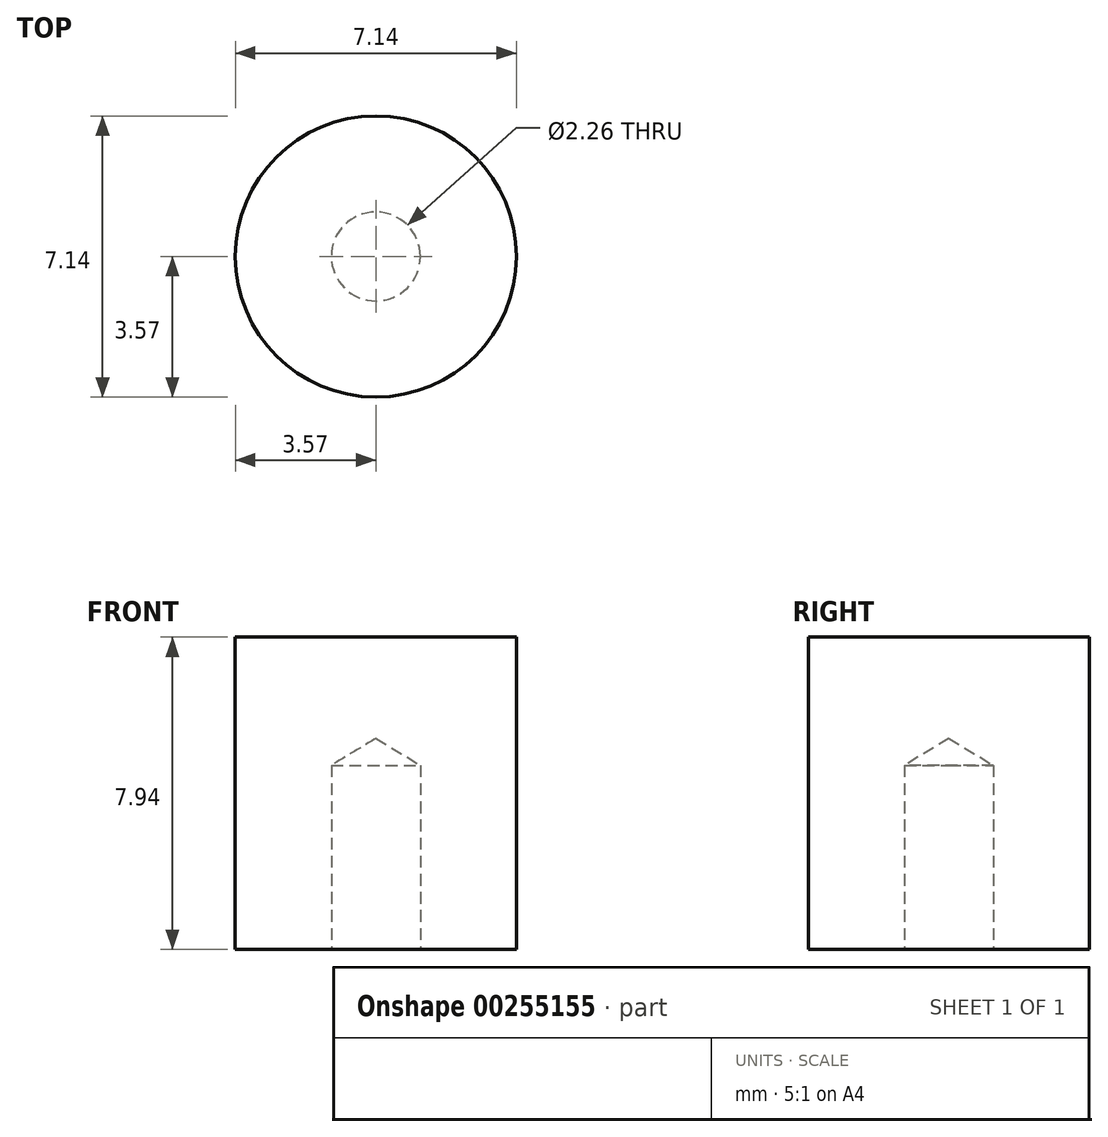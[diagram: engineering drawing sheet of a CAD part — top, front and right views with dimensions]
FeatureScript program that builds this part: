
annotation { "Feature Type Name" : "Feature", "Feature Type Description" : "" }
export const myFeature = defineFeature(function(context is Context, id is Id, definition is map)
    precondition{}
    {
        {
            var Q0;
            Q0=qCreatedBy(makeId("Top.planeOp"),FACE);
            var sketch = newSketch(context, id + "F0", { "sketchPlane" : qUnion([Q0])});
            skCircle(sketch, "E0", {"center": v(0, 0) * mm, "radius": 3.57 * mm});
            skSolve(sketch);
        }
        {
            var Q0;
            Q0 = qSketchRegion(id + "F0", true);
            extrude(context, id + "F1", {"entities" : qUnion([Q0]), "depth" : 7.94 * mm});
        }
        {
            var Q0;
            Q0=makeQuery(id+"F1.opExtrude","CAP_FACE",FACE,{"disambiguationData":[OSD([sQuery(id+"F0.wireOp",EDGE,"E0")])],"isStart":true});
            var sketch = newSketch(context, id + "F2", { "sketchPlane" : qUnion([Q0])});
            skPoint(sketch, "E1", {"position": v(0, 0) * mm});
            skSolve(sketch);
        }
        {
            var Q0;
            Q0=sQuery(id+"F2.wireOp",VERTEX,"E1");
            var Q1;
            Q1=makeQuery(id+"F1.opExtrude","SWEPT_BODY",BODY,{"disambiguationData":[OSD([sQuery(id+"F0.wireOp",EDGE,"E0")])]});
            hole(context, id + "F3", {"style" : HoleStyle.SIMPLE, "endStyle" : HoleEndStyle.BLIND, "standardTappedOrClearance" : lookupTablePath({ "standard" : "ANSI", "engagement" : "75%", "pitch" : "40 tpi", "size" : "#4", "type" : "Tapped" }), "standardBlindInLast" : lookupTablePath({ "standard" : "ANSI", "engagement" : "75%", "pitch" : "40 tpi", "size" : "#4", "type" : "Tapped" }), "holeDiameter" : 2.26 * mm, "showTappedDepth" : true, "holeDepth" : 4.68 * mm, "tappedDepth" : 2.78 * mm, "tapClearance" : 3, "startFromSketch" : true, "locations" : qUnion([Q0]), "scope" : qUnion([Q1]), "majorDiameter" : 2.84 * mm});
        }
    });
